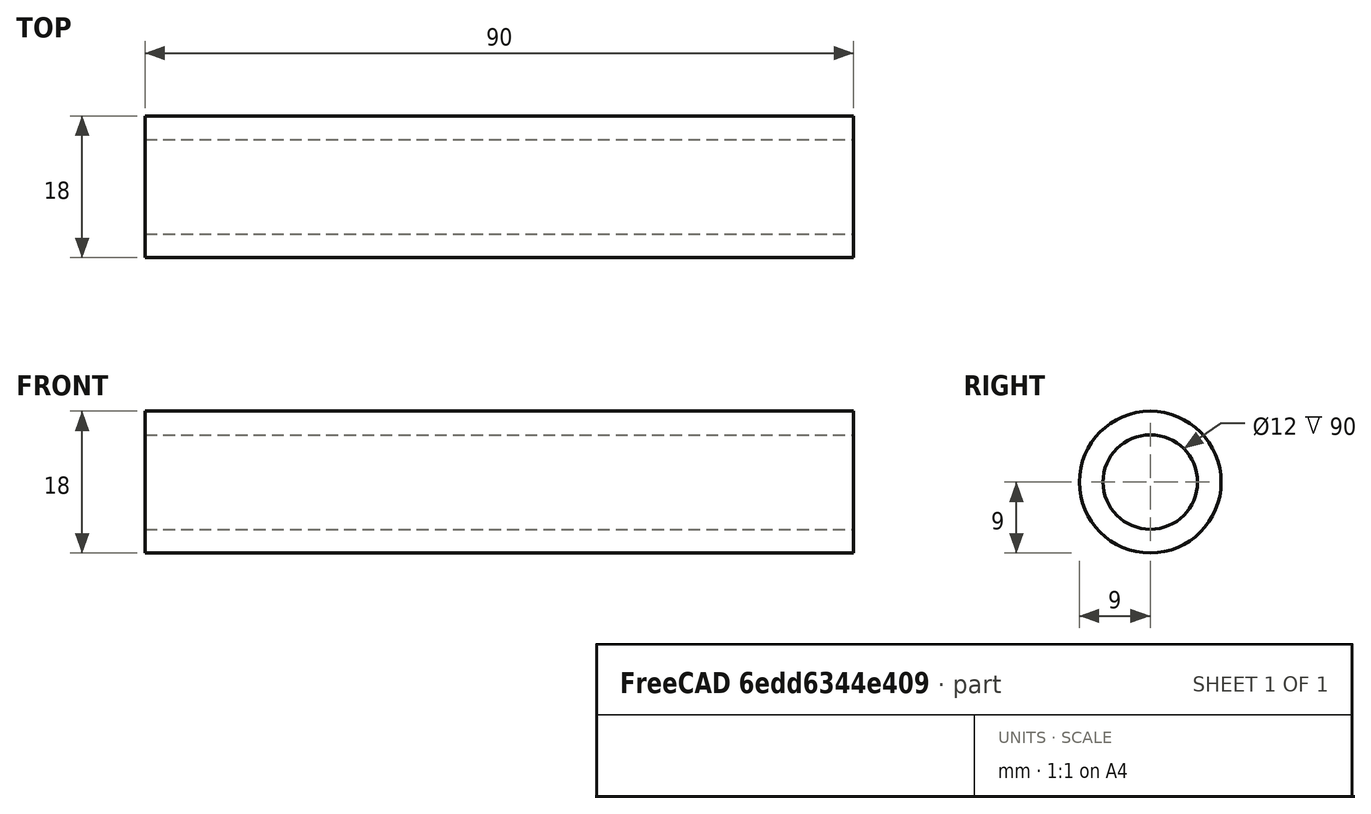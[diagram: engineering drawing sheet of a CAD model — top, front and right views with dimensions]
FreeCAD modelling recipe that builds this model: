
FCSTD DOCUMENT  (FreeCAD 0.19R)
Label: cartridge
License: All rights reserved
LicenseURL: http://en.wikipedia.org/wiki/All_rights_reserved
objects: Sketcher::SketchObject×1, PartDesign::Revolution×1, PartDesign::Body×1
note: 4 computed .brp shape members not serialized (recipe doc carries the construction recipe); baked Part::Feature solids carry a one-line shape summary decoded from their .brp

FEATURE [Sketcher::SketchObject] Sketch
  MapMode = 5
  Support = -> [XY_Plane]
  sketch-geometry (4):
    g0: LineSegment StartX=0 StartY=6 StartZ=0 EndX=90 EndY=6 EndZ=0
    g1: LineSegment StartX=90 StartY=6 StartZ=0 EndX=90 EndY=9 EndZ=0
    g2: LineSegment StartX=90 StartY=9 StartZ=0 EndX=0 EndY=9 EndZ=0
    g3: LineSegment StartX=0 StartY=9 StartZ=0 EndX=0 EndY=6 EndZ=0
  constraints (12):
    c: PointOnObject(g0,g-2)
    c: Horizontal(g0)
    c: Coincident(g1,g0)
    c: Vertical(g1)
    c: Coincident(g2,g1)
    c: Horizontal(g2)
    c: Coincident(g3,g2)
    c: Coincident(g3,g0)
    c: Vertical(g3)
    c: Distance(g-1,g0) = 6
    c: Distance(g3) = 3
    c: Distance(g2) = 90
FEATURE [PartDesign::Revolution] Revolution
  AllowMultiFace = false
  Angle = 360
  Axis = (1,0,0)
  Base = (0,0,0)
  Profile = -> Sketch
  ReferenceAxis = -> X_Axis
FEATURE [PartDesign::Body] Body
  Group = -> [Sketch,Revolution]
  Origin = -> Origin
  Tip = -> Revolution
